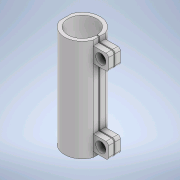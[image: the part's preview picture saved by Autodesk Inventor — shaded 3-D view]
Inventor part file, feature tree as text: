
AUTODESK INVENTOR PART (.ipt)
format: ipt  version: 2020.1 (Build 241239000, 239)  size: 202,752 bytes
history: native  units: mm
features: extrude x5, sketch x5, fillet x1
ambient origin geometry x8: Origin, YZ Plane, XZ Plane, XY Plane, X Axis, Y Axis, Z Axis, Center Point
bodies: Volumenkörper1 (feature_tree)
feature tree (11):
  extrude  "Extrusion1"  Depth=35.0mm
  extrude  "Extrusion2"  Depth=100.0mm
  extrude  "Extrusion3"  Depth=0.5mm
  extrude  "Extrusion4"  Depth=1.0mm
  fillet  "Rundung1"  Radius=10.0mm
  extrude  "Extrusion5"  Depth=5.0mm
  sketch  "Skizze1"  dims[d0=28.0mm d1=35.0mm]
  sketch  "Skizze2"  dims[d2=100.0mm d3=0.0mm d4=8.0mm]
  sketch  "Skizze3"  dims[d5=0.5mm d6=0.5mm]
  sketch  "Skizze4"  dims[d7=1000.0mm d8=0.0mm d9=1.0mm d10=10.0mm]
  sketch  "Skizze5"  dims[d11=1000.0mm d12=0.0mm d13=5.0mm d14=15.0mm d15=15.0mm d16=15.0mm d17=0.0mm d18=2.5mm d19=7.5mm d20=0.0mm d21=7.5mm d22=90.0deg d23=10.0mm d24=7.5mm d25=0.0mm d26=7.5mm d27=90.0deg d28=10.0mm d29=100.0mm d30=0.0mm]
